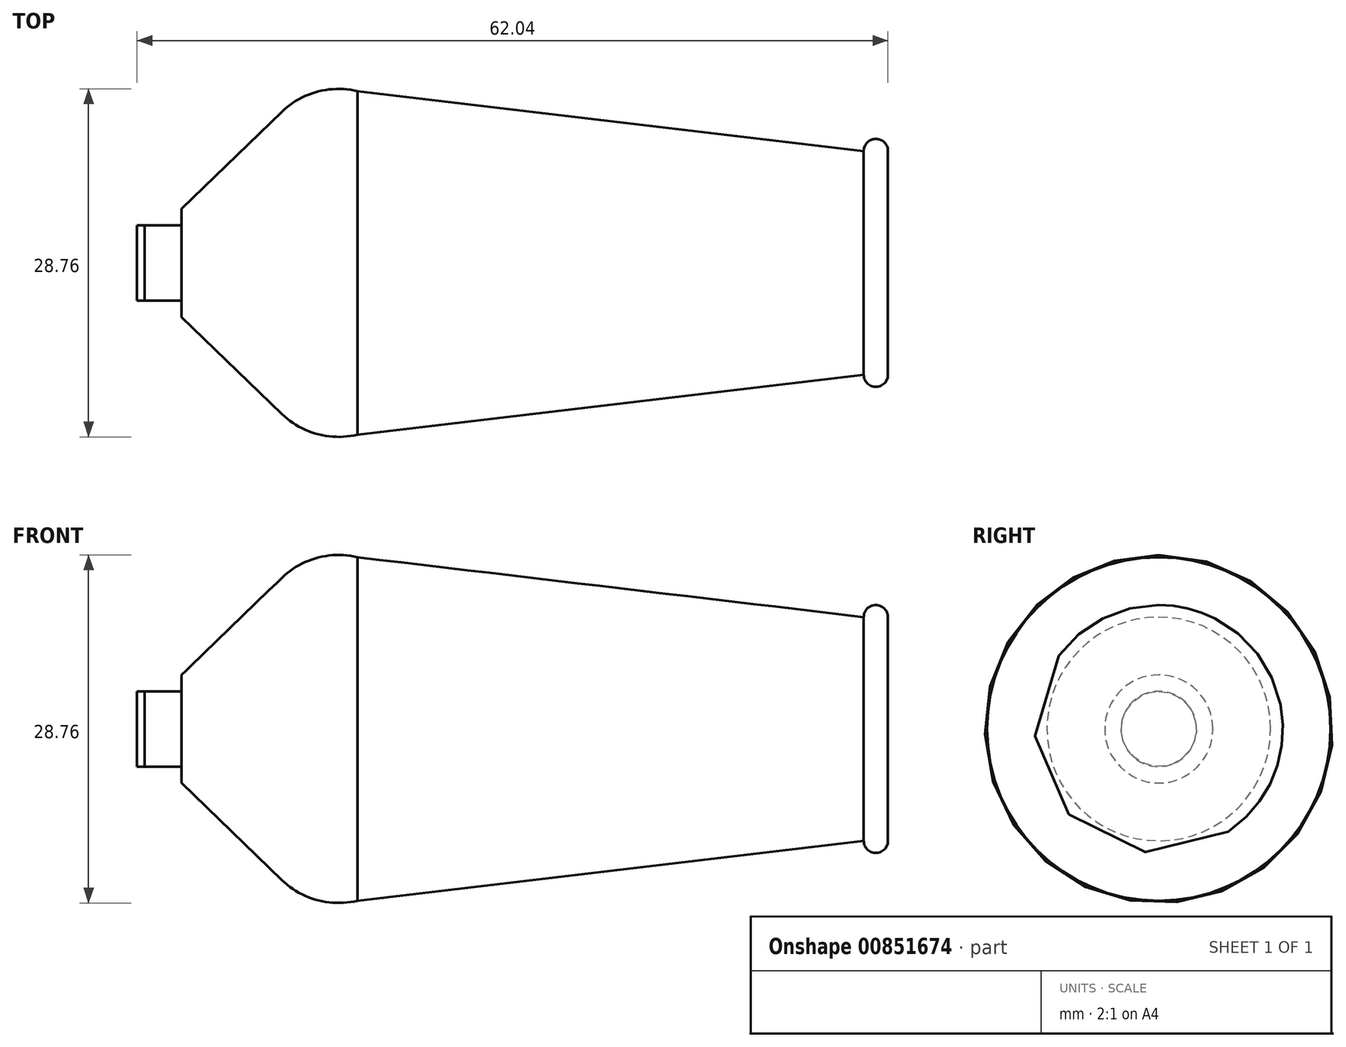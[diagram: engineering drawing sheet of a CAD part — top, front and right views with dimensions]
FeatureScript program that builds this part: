
annotation { "Feature Type Name" : "Feature", "Feature Type Description" : "" }
export const myFeature = defineFeature(function(context is Context, id is Id, definition is map)
    precondition{}
    {
        {
            var Q0;
            Q0=qCreatedBy(makeId("Front.planeOp"),FACE);
            var sketch = newSketch(context, id + "F0", { "sketchPlane" : qUnion([Q0])});
            skLineSegment(sketch, "E0", {"start": v(0, 0) * mm, "end": v(0, 0) * mm});
            skLineSegment(sketch, "E1", {"start": v(4.51, 3.12) * mm, "end": v(25.13, 3.12) * mm});
            skLineSegment(sketch, "E2", {"start": v(0, 3.12) * mm, "end": v(28.18, 3.12) * mm});
            skLineSegment(sketch, "E3", {"start": v(110.32, 3.12) * mm, "end": v(110.32, 0) * mm});
            skArc(sketch, "E4", {"start": v(23.18, 3.4) * mm, "mid": v(24.14, 3.15) * mm, "end": v(25.13, 3.12) * mm});
            skLineSegment(sketch, "E5", {"start": v(28.18, 4.47) * mm, "end": v(36.46, 12.48) * mm});
            skPoint(sketch, "E6.start.orphan", {"position": v(33.62, 12.48) * mm});
            skArc(sketch, "E7", {"start": v(36.46, 12.48) * mm, "mid": v(39.36, 14.14) * mm, "end": v(42.7, 14.19) * mm});
            skLineSegment(sketch, "E8", {"start": v(42.7, 14.19) * mm, "end": v(84.54, 9.24) * mm});
            skLineSegment(sketch, "E9", {"start": v(84.54, 9.24) * mm, "end": v(84.54, 0) * mm});
            skLineSegment(sketch, "E10", {"start": v(86.54, 9.24) * mm, "end": v(86.54, 0) * mm});
            skArc(sketch, "E11", {"start": v(86.54, 9.24) * mm, "mid": v(85.54, 10.25) * mm, "end": v(84.54, 9.24) * mm});
            skPoint(sketch, "E12.orphan", {"position": v(41.14, 14.38) * mm});
            skLineSegment(sketch, "E13", {"start": v(25.13, 3.12) * mm, "end": v(25.13, 0) * mm});
            skLineSegment(sketch, "E14", {"start": v(28.18, 4.47) * mm, "end": v(28.18, 0) * mm});
            skLineSegment(sketch, "E15", {"start": v(36.46, 12.48) * mm, "end": v(36.46, 0) * mm});
            skLineSegment(sketch, "E16", {"start": v(41.14, 14.38) * mm, "end": v(41.14, 0) * mm});
            skLineSegment(sketch, "E17", {"start": v(42.7, 14.19) * mm, "end": v(42.7, 0) * mm});
            skLineSegment(sketch, "E18", {"start": v(85.54, 10.25) * mm, "end": v(85.54, 0) * mm});
            skLineSegment(sketch, "E19", {"start": v(0, 0) * mm, "end": v(86.54, 0) * mm});
            skLineSegment(sketch, "E20.trimOffspring", {"start": v(86.54, 3.12) * mm, "end": v(110.32, 3.12) * mm});
            skSolve(sketch);
        }
        {
            var Q0;
            Q0 = qSketchRegion(id + "F0", true);
            var Q1;
            Q1=sQuery(id+"F0.wireOp",EDGE,"E19");
            revolve(context, id + "F1", {"surfaceOperationType" : NewSurfaceOperationType.NEW, "entities" : qUnion([Q0]), "axis" : qUnion([Q1]), "revolveType" : RevolveType.FULL});
        }
    });
